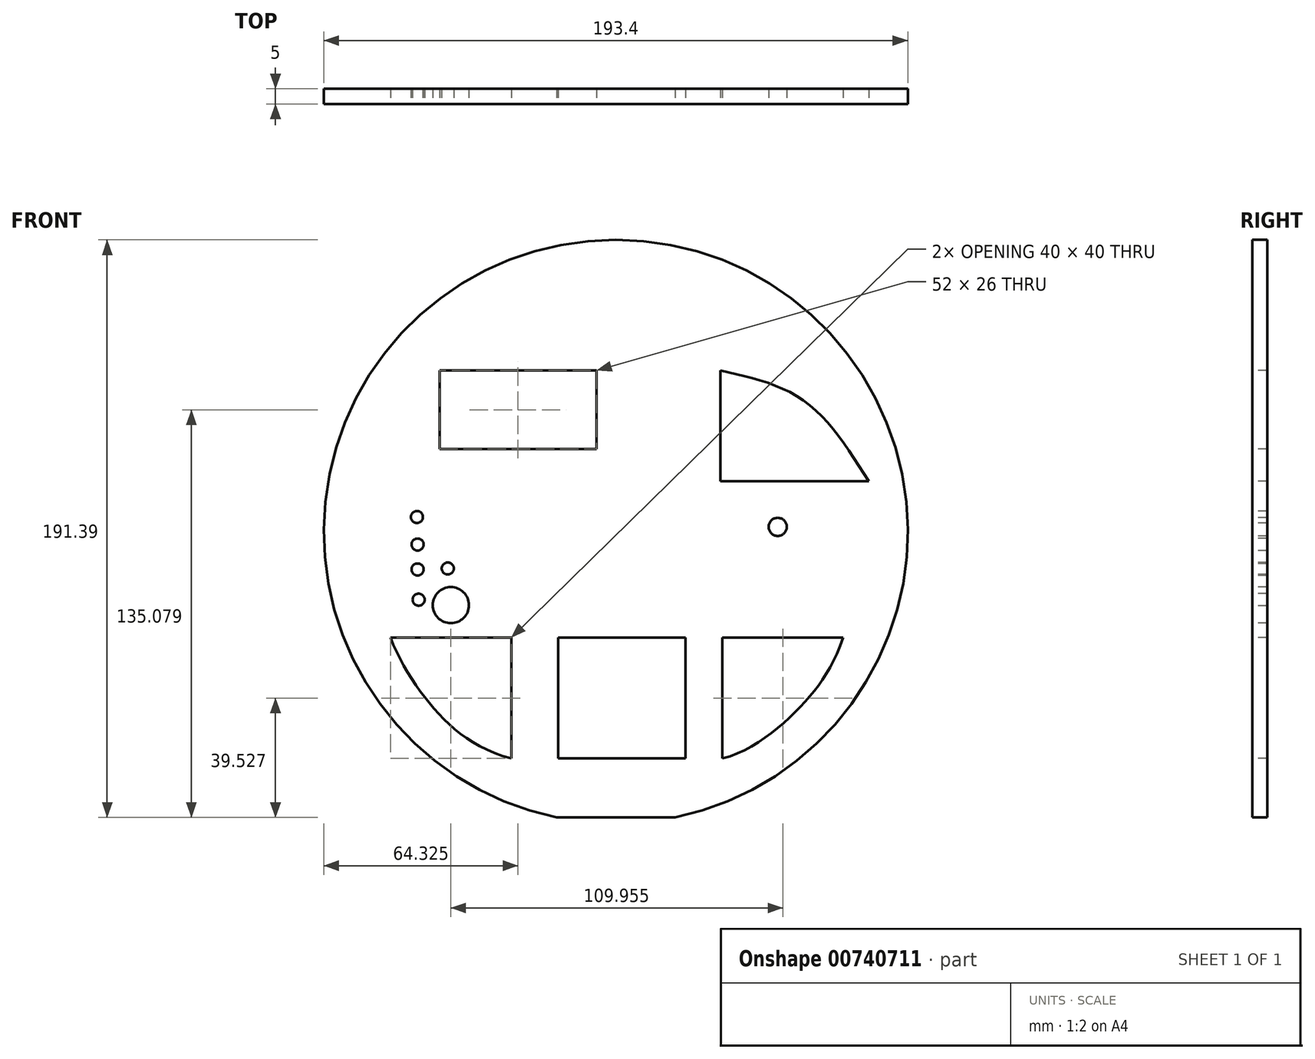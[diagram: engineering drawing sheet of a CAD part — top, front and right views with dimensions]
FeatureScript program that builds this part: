
annotation { "Feature Type Name" : "Feature", "Feature Type Description" : "" }
export const myFeature = defineFeature(function(context is Context, id is Id, definition is map)
    precondition{}
    {
        {
            var Q0;
            Q0=qCreatedBy(makeId("Front.planeOp"),FACE);
            var sketch = newSketch(context, id + "F0", { "sketchPlane" : qUnion([Q0])});
            skArc(sketch, "E0", {"start": v(153.73, 5.14) * mm, "mid": v(134.1, 196.53) * mm, "end": v(114.49, 5.14) * mm});
            skLineSegment(sketch, "E1", {"start": v(37.7, 92.36) * mm, "end": v(230.52, 92.36) * mm});
            skLineSegment(sketch, "E2", {"start": v(37.94, 109.98) * mm, "end": v(230.28, 109.98) * mm});
            skLineSegment(sketch, "E3", {"start": v(114.49, 5.14) * mm, "end": v(153.73, 5.14) * mm});
            skLineSegment(sketch, "E4.bottom", {"start": v(75.73, 153.22) * mm, "end": v(127.73, 153.22) * mm});
            skLineSegment(sketch, "E4.top", {"start": v(75.73, 127.22) * mm, "end": v(127.73, 127.22) * mm});
            skLineSegment(sketch, "E4.left", {"start": v(75.73, 153.22) * mm, "end": v(75.73, 127.22) * mm});
            skLineSegment(sketch, "E4.right", {"start": v(127.73, 153.22) * mm, "end": v(127.73, 127.22) * mm});
            skLineSegment(sketch, "E5", {"start": v(59.48, 64.67) * mm, "end": v(99.48, 64.67) * mm});
            skLineSegment(sketch, "E6", {"start": v(99.48, 64.67) * mm, "end": v(99.48, 24.67) * mm});
            skLineSegment(sketch, "E7", {"start": v(209.43, 64.67) * mm, "end": v(169.43, 64.67) * mm});
            skLineSegment(sketch, "E8", {"start": v(169.43, 64.67) * mm, "end": v(169.43, 24.67) * mm});
            skLineSegment(sketch, "E9", {"start": v(115.02, 64.67) * mm, "end": v(157.25, 64.67) * mm});
            skLineSegment(sketch, "E10", {"start": v(157.25, 64.67) * mm, "end": v(157.25, 24.67) * mm});
            skLineSegment(sketch, "E11", {"start": v(115.02, 64.67) * mm, "end": v(115.02, 24.67) * mm});
            skLineSegment(sketch, "E12", {"start": v(115.02, 24.67) * mm, "end": v(157.25, 24.67) * mm});
            skFitSpline(sketch, "E13", {"points": [v(59.48, 64.67) * mm, v(74.55, 40.49) * mm, v(99.48, 24.67) * mm], "startDerivative": vector(21.97, -54.84) * mm, "endDerivative": vector(68.04, -18.73) * mm});
            skFitSpline(sketch, "E14", {"points": [v(169.43, 24.67) * mm, v(194.7, 41.3) * mm, v(209.43, 64.67) * mm], "startDerivative": vector(57.63, 14.8) * mm, "endDerivative": vector(22.95, 64.37) * mm});
            skLineSegment(sketch, "E15", {"start": v(168.73, 153.22) * mm, "end": v(168.73, 116.49) * mm});
            skLineSegment(sketch, "E16", {"start": v(168.73, 116.49) * mm, "end": v(217.86, 116.49) * mm});
            skFitSpline(sketch, "E17", {"points": [v(168.73, 153.22) * mm, v(196.34, 143.28) * mm, v(217.86, 116.49) * mm], "startDerivative": vector(61.26, -14.27) * mm, "endDerivative": vector(37.3, -59.44) * mm});
            skCircle(sketch, "E18", {"center": v(68.26, 104.67) * mm, "radius": 2 * mm});
            skCircle(sketch, "E19", {"center": v(68.48, 95.55) * mm, "radius": 2 * mm});
            skCircle(sketch, "E20", {"center": v(68.48, 87.28) * mm, "radius": 2 * mm});
            skCircle(sketch, "E21", {"center": v(68.82, 77.29) * mm, "radius": 2 * mm});
            skCircle(sketch, "E22", {"center": v(78.47, 87.63) * mm, "radius": 2 * mm});
            skCircle(sketch, "E23", {"center": v(79.48, 75.5) * mm, "radius": 6 * mm});
            skPoint(sketch, "E23.centerSnap0", {"position": v(79.48, 64.67) * mm});
            skCircle(sketch, "E24", {"center": v(187.73, 101.41) * mm, "radius": 3 * mm});
            skSolve(sketch);
        }
        {
            var Q0;
            Q0 = qSketchRegion(id + "F0", true);
            extrude(context, id + "F1", {"entities" : qUnion([Q0]), "oppositeDirection" : true, "depth" : 5 * mm, "offsetDistance" : 25 * mm});
        }
        {
            var Q0;
            Q0=sQuery(id+"F0.wireOp",EDGE,"E2");
            var Q1;
            Q1=sQuery(id+"F0.wireOp",EDGE,"E1");
            extrude(context, id + "F2", {"bodyType" : ToolBodyType.SURFACE, "surfaceEntities" : qUnion([Q0, Q1]), "oppositeDirection" : true, "depth" : 2 * mm, "offsetDistance" : 25 * mm});
        }
    });
